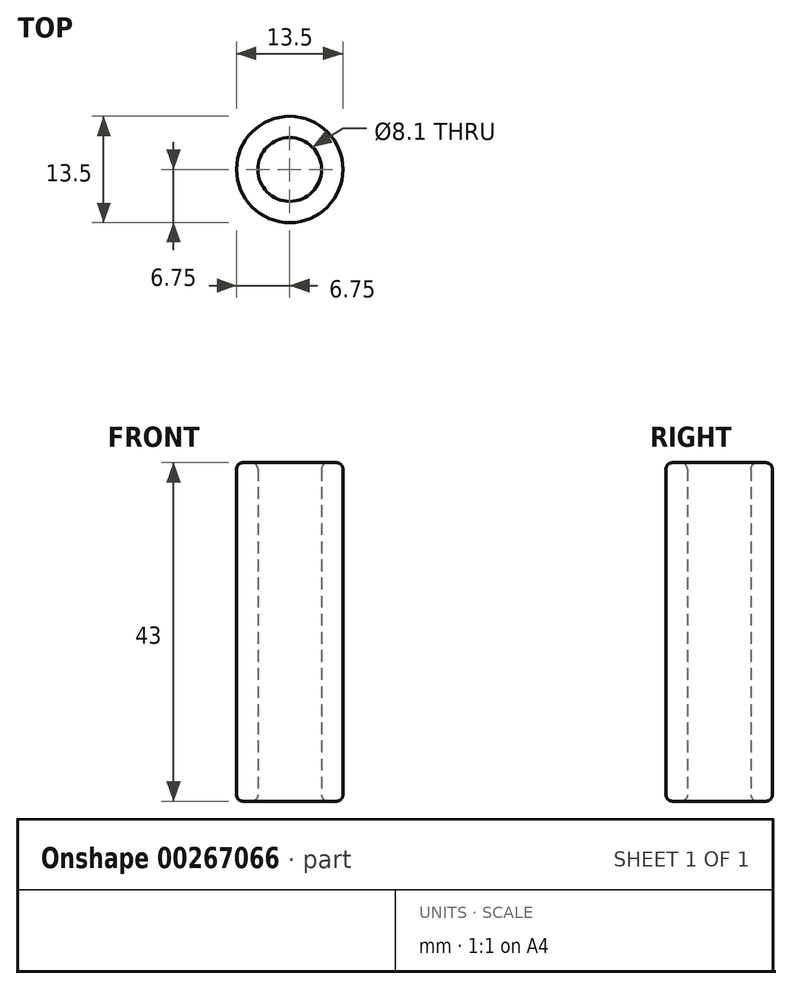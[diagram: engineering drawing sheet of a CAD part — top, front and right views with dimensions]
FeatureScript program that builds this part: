
annotation { "Feature Type Name" : "Feature", "Feature Type Description" : "" }
export const myFeature = defineFeature(function(context is Context, id is Id, definition is map)
    precondition{}
    {
        {
            var Q0;
            Q0=qCreatedBy(makeId("Top.planeOp"),FACE);
            var sketch = newSketch(context, id + "F0", { "sketchPlane" : qUnion([Q0])});
            skCircle(sketch, "E0", {"center": v(0, 0) * mm, "radius": 4.05 * mm});
            skCircle(sketch, "E1", {"center": v(0, 0) * mm, "radius": 6.75 * mm});
            skSolve(sketch);
        }
        {
            var Q0;
            Q0=makeQuery(id+"F0.imprint","IMPRINT",FACE,{"disambiguationData":[TD([[makeQuery(id+"F0.imprint","IMPRINT",EDGE,{"derivedFrom":sQuery(id+"F0.wireOp",EDGE,"E0")}),-1.0]])]});
            extrude(context, id + "F1", {"entities" : qUnion([Q0]), "depth" : 43 * mm});
        }
        {
            var Q0;
            Q0=makeQuery(id+"F1.opExtrude","CAP_FACE",FACE,{"disambiguationData":[OSD([sQuery(id+"F0.wireOp",EDGE,"E0"),sQuery(id+"F0.wireOp",EDGE,"E1")])],"isStart":false});
            var Q1;
            Q1=makeQuery(id+"F1.opExtrude","CAP_FACE",FACE,{"disambiguationData":[OSD([sQuery(id+"F0.wireOp",EDGE,"E0"),sQuery(id+"F0.wireOp",EDGE,"E1")])],"isStart":true});
            fillet(context, id + "F2", {"entities" : qUnion([Q0, Q1]), "radius" : 0.8 * mm, "tangentPropagation" : true, "allowEdgeOverflow" : false});
        }
    });
